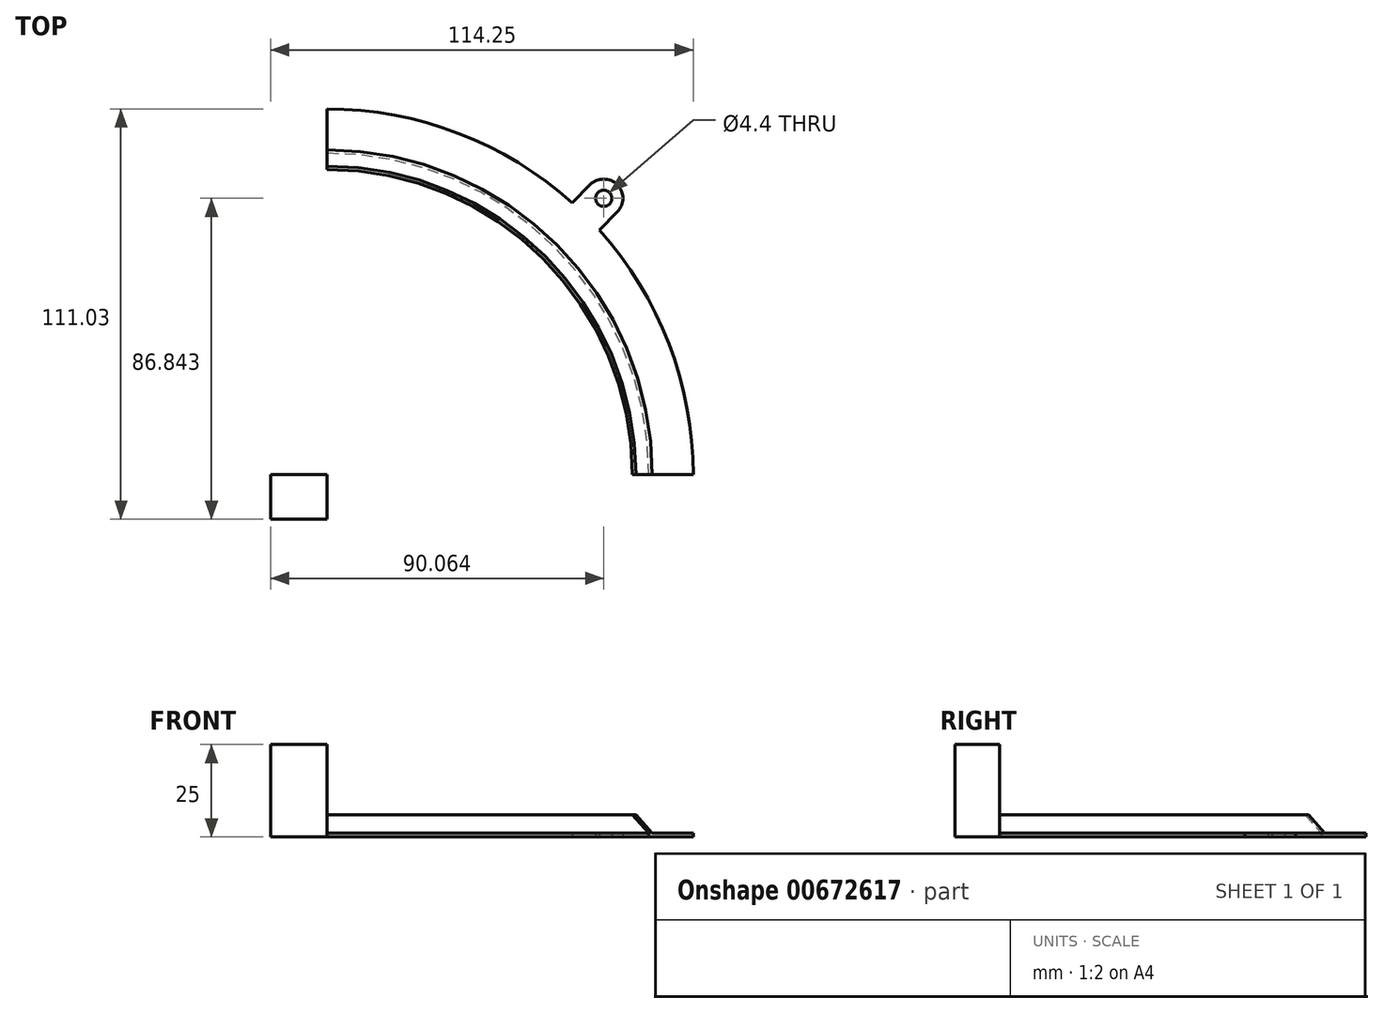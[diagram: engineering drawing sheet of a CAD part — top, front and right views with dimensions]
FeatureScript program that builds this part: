
annotation { "Feature Type Name" : "Feature", "Feature Type Description" : "" }
export const myFeature = defineFeature(function(context is Context, id is Id, definition is map)
    precondition{}
    {
        {
            var Q0;
            Q0=qCreatedBy(makeId("Top.planeOp"),FACE);
            var sketch = newSketch(context, id + "F0", { "sketchPlane" : qUnion([Q0])});
            skCircle(sketch, "E0", {"center": v(95.8, 90.85) * mm, "radius": 2.2 * mm});
            skArc(sketch, "E1", {"start": v(99.47, 87.18) * mm, "mid": v(99.47, 94.53) * mm, "end": v(92.12, 94.53) * mm});
            skLineSegment(sketch, "E2.bottom", {"start": v(92.12, 94.53) * mm, "end": v(87.21, 89.62) * mm});
            skLineSegment(sketch, "E2.top", {"start": v(99.47, 87.18) * mm, "end": v(94.57, 82.27) * mm});
            skPoint(sketch, "E2.middle", {"position": v(0, 0) * mm});
            skLineSegment(sketch, "E3", {"start": v(21, 103.04) * mm, "end": v(21, 115.04) * mm});
            skLineSegment(sketch, "E4", {"start": v(107.98, 16.05) * mm, "end": v(119.98, 16.05) * mm});
            skArc(sketch, "E5", {"start": v(107.98, 16.05) * mm, "mid": v(82.5, 77.56) * mm, "end": v(21, 103.04) * mm});
            skArc(sketch, "E6", {"start": v(87.21, 89.62) * mm, "mid": v(56.46, 108.47) * mm, "end": v(21, 115.04) * mm});
            skArc(sketch, "E7.trimOffspring", {"start": v(119.98, 16.05) * mm, "mid": v(113.4, 51.52) * mm, "end": v(94.57, 82.27) * mm});
            skLineSegment(sketch, "E8.bottom", {"start": v(21, 16.05) * mm, "end": v(5.73, 16.05) * mm});
            skLineSegment(sketch, "E8.top", {"start": v(21, 4.01) * mm, "end": v(5.73, 4.01) * mm});
            skLineSegment(sketch, "E8.left", {"start": v(21, 16.05) * mm, "end": v(21, 4.01) * mm});
            skLineSegment(sketch, "E8.right", {"start": v(5.73, 16.05) * mm, "end": v(5.73, 4.01) * mm});
            skSolve(sketch);
        }
        {
            var Q0;
            Q0=makeQuery(id+"F0.imprint","IMPRINT",FACE,{"disambiguationData":[TD([[makeQuery(id+"F0.imprint","IMPRINT",EDGE,{"derivedFrom":sQuery(id+"F0.wireOp",EDGE,"E0")}),-1.0]])]});
            var Q1;
            Q1=makeQuery(id+"F0.imprint","IMPRINT",FACE,{"disambiguationData":[TD([[makeQuery(id+"F0.imprint","IMPRINT",EDGE,{"derivedFrom":sQuery(id+"F0.wireOp",EDGE,"LjHXDUb4-ZFo0-YAoy-zGkI-DgYwUBjRm7BI.bottom")}),1.0]])]});
            extrude(context, id + "F1", {"entities" : qUnion([Q0, Q1]), "depth" : 1 * mm, "offsetDistance" : 25 * mm});
        }
        {
            var Q0;
            Q0=makeQuery(id+"F1.opExtrude","SWEPT_FACE",FACE,{"disambiguationData":[OSD([sQuery(id+"F0.wireOp",EDGE,"E4")])]});
            var sketch = newSketch(context, id + "F2", { "sketchPlane" : qUnion([Q0])});
            skLineSegment(sketch, "E9", {"start": v(104.48, 6) * mm, "end": v(108.88, 1) * mm});
            skLineSegment(sketch, "E10", {"start": v(103.58, 6) * mm, "end": v(107.98, 1) * mm});
            skLineSegment(sketch, "E11", {"start": v(103.58, 6) * mm, "end": v(104.48, 6) * mm});
            skLineSegment(sketch, "E12", {"start": v(107.98, 1) * mm, "end": v(108.88, 1) * mm});
            skSolve(sketch);
        }
        {
            var Q0;
            Q0=makeQuery(id+"F0.imprint","IMPRINT",FACE,{"disambiguationData":[TD([[makeQuery(id+"F0.imprint","IMPRINT",EDGE,{"derivedFrom":sQuery(id+"F0.wireOp",EDGE,"E8.bottom")}),1.0]])]});
            extrude(context, id + "F3", {"entities" : qUnion([Q0]), "depth" : 25 * mm, "offsetDistance" : 25 * mm});
        }
        {
            var Q0;
            Q0=makeQuery(id+"F2.imprint","IMPRINT",FACE,{"disambiguationData":[TD([[makeQuery(id+"F2.imprint","IMPRINT",EDGE,{"derivedFrom":sQuery(id+"F2.wireOp",EDGE,"E9")}),-1.0]])]});
            var Q1;
            Q1=makeQuery(id+"F3.opExtrude","SWEPT_EDGE",EDGE,{"disambiguationData":[OSD([sQuery(id+"F0.wireOp",EDGE,"E8.bottom"),sQuery(id+"F0.wireOp",EDGE,"E8.left")])]});
            revolve(context, id + "F4", {"operationType" : NewBodyOperationType.ADD, "entities" : qUnion([Q0]), "axis" : qUnion([Q1]), "revolveType" : RevolveType.ONE_DIRECTION, "oppositeDirection" : true, "angle" : 90 * degree});
        }
    });
